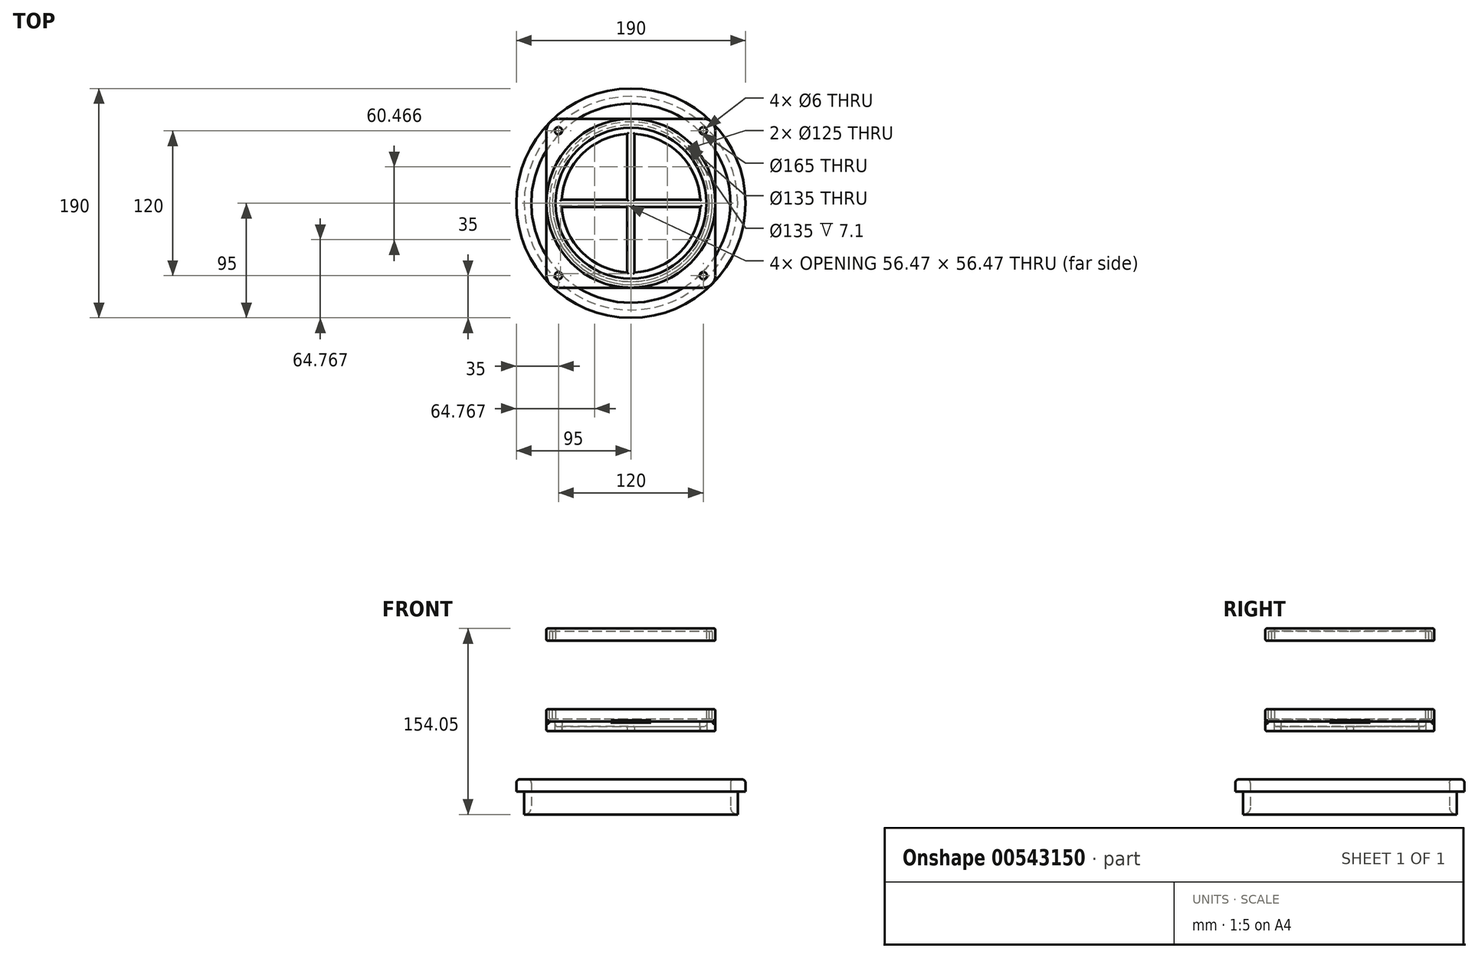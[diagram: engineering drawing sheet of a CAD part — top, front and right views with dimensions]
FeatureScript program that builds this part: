
annotation { "Feature Type Name" : "Feature", "Feature Type Description" : "" }
export const myFeature = defineFeature(function(context is Context, id is Id, definition is map)
    precondition{}
    {
        {
            var Q0;
            Q0=qCreatedBy(makeId("Top.planeOp"),FACE);
            var sketch = newSketch(context, id + "F0", { "sketchPlane" : qUnion([Q0])});
            skLineSegment(sketch, "E0.bottom", {"start": v(-60, 70) * mm, "end": v(60, 70) * mm});
            skLineSegment(sketch, "E0.top", {"start": v(-60, -70) * mm, "end": v(60, -70) * mm});
            skLineSegment(sketch, "E0.left", {"start": v(-70, 60) * mm, "end": v(-70, -60) * mm});
            skLineSegment(sketch, "E0.right", {"start": v(70, 60) * mm, "end": v(70, -60) * mm});
            skCircle(sketch, "E1", {"center": v(-60, 60) * mm, "radius": 3 * mm});
            skCircle(sketch, "E2.MirrorC", {"center": v(60, 60) * mm, "radius": 3 * mm});
            skCircle(sketch, "E3.MirrorC", {"center": v(60, -60) * mm, "radius": 3 * mm});
            skCircle(sketch, "E4.MirrorC", {"center": v(-60, -60) * mm, "radius": 3 * mm});
            skPoint(sketch, "E5.visualSharp", {"position": v(-70, -70) * mm});
            skArc(sketch, "E5.filletArc", {"start": v(-70, -60) * mm, "mid": v(-67.07, -67.07) * mm, "end": v(-60, -70) * mm});
            skPoint(sketch, "E6.visualSharp", {"position": v(-70, 70) * mm});
            skArc(sketch, "E6.filletArc", {"start": v(-60, 70) * mm, "mid": v(-67.07, 67.07) * mm, "end": v(-70, 60) * mm});
            skPoint(sketch, "E7.visualSharp", {"position": v(70, 70) * mm});
            skArc(sketch, "E7.filletArc", {"start": v(70, 60) * mm, "mid": v(67.07, 67.07) * mm, "end": v(60, 70) * mm});
            skPoint(sketch, "E8.visualSharp", {"position": v(70, -70) * mm});
            skArc(sketch, "E8.filletArc", {"start": v(60, -70) * mm, "mid": v(67.07, -67.07) * mm, "end": v(70, -60) * mm});
            skSolve(sketch);
        }
        {
            var Q0;
            Q0 = qSketchRegion(id + "F0", true);
            extrude(context, id + "F1", {"entities" : qUnion([Q0]), "depth" : 8 * mm, "offsetDistance" : 25 * mm});
        }
        {
            var Q0;
            Q0=makeQuery(id+"F1.opExtrude","CAP_FACE",FACE,{"disambiguationData":[OSD([sQuery(id+"F0.wireOp",EDGE,"E0.bottom"),sQuery(id+"F0.wireOp",EDGE,"E0.top"),sQuery(id+"F0.wireOp",EDGE,"E0.left"),sQuery(id+"F0.wireOp",EDGE,"E0.right"),sQuery(id+"F0.wireOp",EDGE,"E1"),sQuery(id+"F0.wireOp",EDGE,"E2.MirrorC"),sQuery(id+"F0.wireOp",EDGE,"E3.MirrorC"),sQuery(id+"F0.wireOp",EDGE,"E4.MirrorC"),sQuery(id+"F0.wireOp",EDGE,"E5.filletArc"),sQuery(id+"F0.wireOp",EDGE,"E6.filletArc"),sQuery(id+"F0.wireOp",EDGE,"E7.filletArc"),sQuery(id+"F0.wireOp",EDGE,"E8.filletArc"),sQuery(id+"F0.wireOp",EDGE,"JWdlXrcp-rO1S-G7ss-JCTR-8tZBUIbzlGE1")])],"isStart":false});
            var sketch = newSketch(context, id + "F2", { "sketchPlane" : qUnion([Q0])});
            skCircle(sketch, "E9", {"center": v(0, 0) * mm, "radius": 70 * mm});
            skCircle(sketch, "E10", {"center": v(0, 0) * mm, "radius": 62.5 * mm});
            skSolve(sketch);
        }
        {
            var Q0;
            Q0 = qSketchRegion(id + "F2", true);
            extrude(context, id + "F3", {"entities" : qUnion([Q0]), "operationType" : NewBodyOperationType.ADD, "depth" : 10 * mm, "offsetDistance" : 25 * mm});
        }
        {
            var Q0;
            Q0=makeQuery(id+"F2.imprint","IMPRINT",FACE,{"disambiguationData":[TD([[makeQuery(id+"F2.imprint","IMPRINT",EDGE,{"derivedFrom":sQuery(id+"F2.wireOp",EDGE,"E10")}),1.0]])]});
            var sketch = newSketch(context, id + "F4", { "sketchPlane" : qUnion([Q0])});
            skCircle(sketch, "E11", {"center": v(0, 0) * mm, "radius": 62.5 * mm});
            skSolve(sketch);
        }
        {
            var Q0;
            Q0 = qSketchRegion(id + "F4", true);
            extrude(context, id + "F5", {"entities" : qUnion([Q0]), "operationType" : NewBodyOperationType.REMOVE, "oppositeDirection" : true, "depth" : 25 * mm, "offsetDistance" : 25 * mm});
        }
        {
            var Q0;
            Q0=makeQuery(id+"F3.opExtrude","CAP_FACE",FACE,{"disambiguationData":[OSD([sQuery(id+"F2.wireOp",EDGE,"E9"),sQuery(id+"F2.wireOp",EDGE,"E10")])],"isStart":false});
            var sketch = newSketch(context, id + "F6", { "sketchPlane" : qUnion([Q0])});
            skCircle(sketch, "E12", {"center": v(0, 0) * mm, "radius": 67.5 * mm});
            skCircle(sketch, "E13", {"center": v(0, 0) * mm, "radius": 65 * mm});
            skSolve(sketch);
        }
        {
            var Q0;
            Q0 = qSketchRegion(id + "F6", true);
            extrude(context, id + "F7", {"entities" : qUnion([Q0]), "operationType" : NewBodyOperationType.REMOVE, "oppositeDirection" : true, "depth" : 8 * mm, "offsetDistance" : 25 * mm});
        }
        {
            var Q0;
            Q0=makeQuery(id+"F3.opExtrude","CAP_EDGE",EDGE,{"disambiguationData":[OSD([sQuery(id+"F2.wireOp",EDGE,"E9")])],"isStart":false});
            var Q1;
            Q1=makeQuery(id+"F7.boolean.opBoolean","COPY",EDGE,{"derivedFrom":makeQuery(id+"F7.opExtrude","CAP_EDGE",EDGE,{"disambiguationData":[OSD([sQuery(id+"F6.wireOp",EDGE,"E12")])],"isStart":true})});
            var Q2;
            Q2=makeQuery(id+"F7.boolean.opBoolean","COPY",EDGE,{"derivedFrom":makeQuery(id+"F7.opExtrude","CAP_EDGE",EDGE,{"disambiguationData":[OSD([sQuery(id+"F6.wireOp",EDGE,"E13")])],"isStart":true})});
            var Q3;
            Q3=makeQuery(id+"F3.opExtrude","CAP_EDGE",EDGE,{"disambiguationData":[OSD([sQuery(id+"F2.wireOp",EDGE,"E10")])],"isStart":false});
            var Q4;
            {var subQ0=sQuery(id+"F0.wireOp",EDGE,"E6.filletArc");var subQ1=sQuery(id+"F0.wireOp",EDGE,"E0.left");Q4=makeQuery(id+"F3.boolean.opBoolean","SPLIT",EDGE,{"disambiguationData":[TD([makeQuery(id+"F1.opExtrude","SWEPT_FACE",FACE,{"disambiguationData":[OSD([subQ0])]})])],"derivedFrom":makeQuery(id+"F1.opExtrude","CAP_EDGE",EDGE,{"disambiguationData":[OSD([subQ1])],"isStart":false})});}
            var Q5;
            {var subQ0=sQuery(id+"F0.wireOp",EDGE,"E0.left");var subQ1=sQuery(id+"F0.wireOp",EDGE,"E0.top");var subQ2=sQuery(id+"F2.wireOp",EDGE,"E9");Q5=makeQuery(id+"F3.boolean.opBoolean","SPLIT",EDGE,{"disambiguationData":[TD([makeQuery(id+"F1.opExtrude","CAP_FACE",FACE,{"disambiguationData":[OSD([sQuery(id+"F0.wireOp",EDGE,"E0.bottom"),subQ1,subQ0,sQuery(id+"F0.wireOp",EDGE,"E0.right"),sQuery(id+"F0.wireOp",EDGE,"E1"),sQuery(id+"F0.wireOp",EDGE,"E2.MirrorC"),sQuery(id+"F0.wireOp",EDGE,"E3.MirrorC"),sQuery(id+"F0.wireOp",EDGE,"E4.MirrorC"),sQuery(id+"F0.wireOp",EDGE,"E5.filletArc"),sQuery(id+"F0.wireOp",EDGE,"E6.filletArc"),sQuery(id+"F0.wireOp",EDGE,"E7.filletArc"),sQuery(id+"F0.wireOp",EDGE,"E8.filletArc")])],"isStart":false}),makeQuery(id+"F1.opExtrude","SWEPT_FACE",FACE,{"disambiguationData":[OSD([subQ1])]}),makeQuery(id+"F1.opExtrude","SWEPT_FACE",FACE,{"disambiguationData":[OSD([subQ0])]}),makeQuery(id+"F3.opExtrude","SWEPT_FACE",FACE,{"disambiguationData":[OSD([subQ2])]})])],"derivedFrom":makeQuery(id+"F3.opExtrude","CAP_EDGE",EDGE,{"disambiguationData":[OSD([subQ2])],"isStart":true})});}
            var Q6;
            Q6=makeQuery(id+"F1.opExtrude","CAP_FACE",FACE,{"disambiguationData":[OSD([sQuery(id+"F0.wireOp",EDGE,"E0.bottom"),sQuery(id+"F0.wireOp",EDGE,"E0.top"),sQuery(id+"F0.wireOp",EDGE,"E0.left"),sQuery(id+"F0.wireOp",EDGE,"E0.right"),sQuery(id+"F0.wireOp",EDGE,"E1"),sQuery(id+"F0.wireOp",EDGE,"E2.MirrorC"),sQuery(id+"F0.wireOp",EDGE,"E3.MirrorC"),sQuery(id+"F0.wireOp",EDGE,"E4.MirrorC"),sQuery(id+"F0.wireOp",EDGE,"E5.filletArc"),sQuery(id+"F0.wireOp",EDGE,"E6.filletArc"),sQuery(id+"F0.wireOp",EDGE,"E7.filletArc"),sQuery(id+"F0.wireOp",EDGE,"E8.filletArc")])],"isStart":true});
            var Q7;
            {var subQ0=sQuery(id+"F0.wireOp",EDGE,"E8.filletArc");var subQ1=sQuery(id+"F0.wireOp",EDGE,"E0.top");Q7=makeQuery(id+"F3.boolean.opBoolean","SPLIT",EDGE,{"disambiguationData":[TD([makeQuery(id+"F1.opExtrude","SWEPT_FACE",FACE,{"disambiguationData":[OSD([subQ0])]})])],"derivedFrom":makeQuery(id+"F1.opExtrude","CAP_EDGE",EDGE,{"disambiguationData":[OSD([subQ1])],"isStart":false})});}
            var Q8;
            {var subQ0=sQuery(id+"F0.wireOp",EDGE,"E0.right");var subQ1=sQuery(id+"F0.wireOp",EDGE,"E3.MirrorC");var subQ2=sQuery(id+"F0.wireOp",EDGE,"E0.top");var subQ3=sQuery(id+"F0.wireOp",EDGE,"E8.filletArc");var subQ4=makeQuery(id+"F1.opExtrude","CAP_FACE",FACE,{"disambiguationData":[OSD([sQuery(id+"F0.wireOp",EDGE,"E0.bottom"),subQ2,sQuery(id+"F0.wireOp",EDGE,"E0.left"),subQ0,sQuery(id+"F0.wireOp",EDGE,"E1"),sQuery(id+"F0.wireOp",EDGE,"E2.MirrorC"),subQ1,sQuery(id+"F0.wireOp",EDGE,"E4.MirrorC"),sQuery(id+"F0.wireOp",EDGE,"E5.filletArc"),sQuery(id+"F0.wireOp",EDGE,"E6.filletArc"),sQuery(id+"F0.wireOp",EDGE,"E7.filletArc"),subQ3])],"isStart":false});Q8=makeQuery(id+"F3.boolean.opBoolean","SPLIT",FACE,{"disambiguationData":[TD([makeQuery(id+"F1.opExtrude","SWEPT_FACE",FACE,{"disambiguationData":[OSD([subQ1])]})])],"derivedFrom":subQ4});}
            var Q9;
            {var subQ0=sQuery(id+"F0.wireOp",EDGE,"E4.MirrorC");var subQ1=sQuery(id+"F0.wireOp",EDGE,"E0.left");var subQ2=sQuery(id+"F0.wireOp",EDGE,"E0.top");var subQ3=sQuery(id+"F0.wireOp",EDGE,"E5.filletArc");var subQ4=makeQuery(id+"F1.opExtrude","CAP_FACE",FACE,{"disambiguationData":[OSD([sQuery(id+"F0.wireOp",EDGE,"E0.bottom"),subQ2,subQ1,sQuery(id+"F0.wireOp",EDGE,"E0.right"),sQuery(id+"F0.wireOp",EDGE,"E1"),sQuery(id+"F0.wireOp",EDGE,"E2.MirrorC"),sQuery(id+"F0.wireOp",EDGE,"E3.MirrorC"),subQ0,subQ3,sQuery(id+"F0.wireOp",EDGE,"E6.filletArc"),sQuery(id+"F0.wireOp",EDGE,"E7.filletArc"),sQuery(id+"F0.wireOp",EDGE,"E8.filletArc")])],"isStart":false});Q9=makeQuery(id+"F3.boolean.opBoolean","SPLIT",FACE,{"disambiguationData":[TD([makeQuery(id+"F1.opExtrude","SWEPT_FACE",FACE,{"disambiguationData":[OSD([subQ0])]})])],"derivedFrom":subQ4});}
            var Q10;
            {var subQ0=sQuery(id+"F0.wireOp",EDGE,"E2.MirrorC");var subQ1=sQuery(id+"F0.wireOp",EDGE,"E7.filletArc");var subQ2=sQuery(id+"F0.wireOp",EDGE,"E0.right");var subQ3=sQuery(id+"F0.wireOp",EDGE,"E0.bottom");var subQ4=makeQuery(id+"F1.opExtrude","CAP_FACE",FACE,{"disambiguationData":[OSD([subQ3,sQuery(id+"F0.wireOp",EDGE,"E0.top"),sQuery(id+"F0.wireOp",EDGE,"E0.left"),subQ2,sQuery(id+"F0.wireOp",EDGE,"E1"),subQ0,sQuery(id+"F0.wireOp",EDGE,"E3.MirrorC"),sQuery(id+"F0.wireOp",EDGE,"E4.MirrorC"),sQuery(id+"F0.wireOp",EDGE,"E5.filletArc"),sQuery(id+"F0.wireOp",EDGE,"E6.filletArc"),subQ1,sQuery(id+"F0.wireOp",EDGE,"E8.filletArc")])],"isStart":false});Q10=makeQuery(id+"F3.boolean.opBoolean","SPLIT",FACE,{"disambiguationData":[TD([makeQuery(id+"F1.opExtrude","SWEPT_FACE",FACE,{"disambiguationData":[OSD([subQ0])]})])],"derivedFrom":subQ4});}
            var Q11;
            {var subQ0=sQuery(id+"F0.wireOp",EDGE,"E1");var subQ1=sQuery(id+"F0.wireOp",EDGE,"E0.left");var subQ2=sQuery(id+"F0.wireOp",EDGE,"E6.filletArc");var subQ3=sQuery(id+"F0.wireOp",EDGE,"E0.bottom");var subQ4=makeQuery(id+"F1.opExtrude","CAP_FACE",FACE,{"disambiguationData":[OSD([subQ3,sQuery(id+"F0.wireOp",EDGE,"E0.top"),subQ1,sQuery(id+"F0.wireOp",EDGE,"E0.right"),subQ0,sQuery(id+"F0.wireOp",EDGE,"E2.MirrorC"),sQuery(id+"F0.wireOp",EDGE,"E3.MirrorC"),sQuery(id+"F0.wireOp",EDGE,"E4.MirrorC"),sQuery(id+"F0.wireOp",EDGE,"E5.filletArc"),subQ2,sQuery(id+"F0.wireOp",EDGE,"E7.filletArc"),sQuery(id+"F0.wireOp",EDGE,"E8.filletArc")])],"isStart":false});Q11=makeQuery(id+"F3.boolean.opBoolean","SPLIT",FACE,{"disambiguationData":[TD([makeQuery(id+"F1.opExtrude","SWEPT_FACE",FACE,{"disambiguationData":[OSD([subQ0])]})])],"derivedFrom":subQ4});}
            fillet(context, id + "F8", {"entities" : qUnion([Q0, Q1, Q2, Q3, Q4, Q5, Q6, Q7, Q8, Q9, Q10, Q11]), "tangentPropagation" : true, "radius" : 1 * mm, "defaultsChanged" : false, "vertexSettings" : [], "allowEdgeOverflow" : false});
        }
        {
            var Q0;
            Q0=makeQuery(id+"F7.boolean.opBoolean","COPY",EDGE,{"derivedFrom":makeQuery(id+"F7.opExtrude","CAP_EDGE",EDGE,{"disambiguationData":[OSD([sQuery(id+"F6.wireOp",EDGE,"E12")])],"isStart":false})});
            var Q1;
            Q1=makeQuery(id+"F7.boolean.opBoolean","COPY",EDGE,{"derivedFrom":makeQuery(id+"F7.opExtrude","CAP_EDGE",EDGE,{"disambiguationData":[OSD([sQuery(id+"F6.wireOp",EDGE,"E13")])],"isStart":false})});
            fillet(context, id + "F9", {"entities" : qUnion([Q0, Q1]), "tangentPropagation" : true, "radius" : 0.9 * mm, "defaultsChanged" : true, "vertexSettings" : [], "allowEdgeOverflow" : false});
        }
        {
            var Q0;
            Q0=qCreatedBy(makeId("Top.planeOp"),FACE);
            cPlane(context, id + "F10", {"entities" : qUnion([Q0]), "cplaneType" : CPlaneType.OFFSET, "offset" : 75 * mm, "width" : 150 * mm, "height" : 150 * mm});
        }
        {
            var Q0;
            Q0=qCreatedBy(id+"F10.planeOp",FACE);
            var sketch = newSketch(context, id + "F11", { "sketchPlane" : qUnion([Q0])});
            skCircle(sketch, "E14", {"center": v(0, 0) * mm, "radius": 62.5 * mm});
            skCircle(sketch, "E15", {"center": v(0, 0) * mm, "radius": 70 * mm});
            skSolve(sketch);
        }
        {
            var Q0;
            Q0 = qSketchRegion(id + "F11", true);
            extrude(context, id + "F12", {"entities" : qUnion([Q0]), "depth" : 10 * mm, "offsetDistance" : 25 * mm});
        }
        {
            var Q0;
            Q0=makeQuery(id+"F12.opExtrude","CAP_FACE",FACE,{"disambiguationData":[OSD([sQuery(id+"F11.wireOp",EDGE,"E14"),sQuery(id+"F11.wireOp",EDGE,"E15")])],"isStart":true});
            var sketch = newSketch(context, id + "F13", { "sketchPlane" : qUnion([Q0])});
            skCircle(sketch, "E16", {"center": v(0, 0) * mm, "radius": 65 * mm});
            skCircle(sketch, "E17", {"center": v(0, 0) * mm, "radius": 67.5 * mm});
            skSolve(sketch);
        }
        {
            var Q0;
            Q0 = qSketchRegion(id + "F13", true);
            extrude(context, id + "F14", {"entities" : qUnion([Q0]), "operationType" : NewBodyOperationType.REMOVE, "oppositeDirection" : true, "depth" : 8 * mm, "offsetDistance" : 25 * mm});
        }
        {
            var Q0;
            Q0=makeQuery(id+"F1.opExtrude","CAP_FACE",FACE,{"disambiguationData":[OSD([sQuery(id+"F0.wireOp",EDGE,"E0.bottom"),sQuery(id+"F0.wireOp",EDGE,"E0.top"),sQuery(id+"F0.wireOp",EDGE,"E0.left"),sQuery(id+"F0.wireOp",EDGE,"E0.right"),sQuery(id+"F0.wireOp",EDGE,"E1"),sQuery(id+"F0.wireOp",EDGE,"E2.MirrorC"),sQuery(id+"F0.wireOp",EDGE,"E3.MirrorC"),sQuery(id+"F0.wireOp",EDGE,"E4.MirrorC"),sQuery(id+"F0.wireOp",EDGE,"E5.filletArc"),sQuery(id+"F0.wireOp",EDGE,"E6.filletArc"),sQuery(id+"F0.wireOp",EDGE,"E7.filletArc"),sQuery(id+"F0.wireOp",EDGE,"E8.filletArc")])],"isStart":true});
            var sketch = newSketch(context, id + "F15", { "sketchPlane" : qUnion([Q0])});
            skCircle(sketch, "E18", {"center": v(0, 0) * mm, "radius": 67.5 * mm});
            skArc(sketch, "E19", {"start": v(-57.42, -3) * mm, "mid": v(-40.66, -40.66) * mm, "end": v(-3, -57.42) * mm});
            skLineSegment(sketch, "E20", {"start": v(3, 57.42) * mm, "end": v(3, 3) * mm});
            skLineSegment(sketch, "E21", {"start": v(3, 3) * mm, "end": v(57.42, 3) * mm});
            skLineSegment(sketch, "E22", {"start": v(3, -3) * mm, "end": v(57.42, -3) * mm});
            skLineSegment(sketch, "E23.trimOffspring", {"start": v(3, -3) * mm, "end": v(3, -57.42) * mm});
            skLineSegment(sketch, "E24.MirrorCS", {"start": v(-3, -3) * mm, "end": v(-3, -57.42) * mm});
            skLineSegment(sketch, "E25.MirrorCS", {"start": v(-3, -3) * mm, "end": v(-57.42, -3) * mm});
            skLineSegment(sketch, "E26.MirrorCS", {"start": v(-3, 3) * mm, "end": v(-57.42, 3) * mm});
            skLineSegment(sketch, "E27.MirrorCS", {"start": v(-3, 57.42) * mm, "end": v(-3, 3) * mm});
            skArc(sketch, "E28.trimOffspring", {"start": v(-3, 57.42) * mm, "mid": v(-40.66, 40.66) * mm, "end": v(-57.42, 3) * mm});
            skArc(sketch, "E29.trimOffspring", {"start": v(57.42, 3) * mm, "mid": v(40.66, 40.66) * mm, "end": v(3, 57.42) * mm});
            skArc(sketch, "E30.trimOffspring", {"start": v(3, -57.42) * mm, "mid": v(40.66, -40.66) * mm, "end": v(57.42, -3) * mm});
            skSolve(sketch);
        }
        {
            var Q0;
            Q0 = qSketchRegion(id + "F15", true);
            extrude(context, id + "F16", {"entities" : qUnion([Q0]), "operationType" : NewBodyOperationType.ADD, "oppositeDirection" : true, "depth" : 4 * mm, "offsetDistance" : 25 * mm});
        }
        {
            var Q0;
            Q0=makeQuery(id+"F16.opExtrude","CAP_FACE",FACE,{"disambiguationData":[OSD([sQuery(id+"F15.wireOp",EDGE,"E18"),sQuery(id+"F15.wireOp",EDGE,"E19"),sQuery(id+"F15.wireOp",EDGE,"E20"),sQuery(id+"F15.wireOp",EDGE,"E21"),sQuery(id+"F15.wireOp",EDGE,"E22"),sQuery(id+"F15.wireOp",EDGE,"E23.trimOffspring"),sQuery(id+"F15.wireOp",EDGE,"E24.MirrorCS"),sQuery(id+"F15.wireOp",EDGE,"E25.MirrorCS"),sQuery(id+"F15.wireOp",EDGE,"E26.MirrorCS"),sQuery(id+"F15.wireOp",EDGE,"E27.MirrorCS"),sQuery(id+"F15.wireOp",EDGE,"E28.trimOffspring"),sQuery(id+"F15.wireOp",EDGE,"E29.trimOffspring"),sQuery(id+"F15.wireOp",EDGE,"E30.trimOffspring")])],"isStart":false});
            var Q1;
            Q1=makeQuery(id+"F16.boolean.opBoolean","MERGE",FACE,{"derivedFrom":[makeQuery(id+"F1.opExtrude","CAP_FACE",FACE,{"disambiguationData":[OSD([sQuery(id+"F0.wireOp",EDGE,"E0.bottom"),sQuery(id+"F0.wireOp",EDGE,"E0.top"),sQuery(id+"F0.wireOp",EDGE,"E0.left"),sQuery(id+"F0.wireOp",EDGE,"E0.right"),sQuery(id+"F0.wireOp",EDGE,"E1"),sQuery(id+"F0.wireOp",EDGE,"E2.MirrorC"),sQuery(id+"F0.wireOp",EDGE,"E3.MirrorC"),sQuery(id+"F0.wireOp",EDGE,"E4.MirrorC"),sQuery(id+"F0.wireOp",EDGE,"E5.filletArc"),sQuery(id+"F0.wireOp",EDGE,"E6.filletArc"),sQuery(id+"F0.wireOp",EDGE,"E7.filletArc"),sQuery(id+"F0.wireOp",EDGE,"E8.filletArc")])],"isStart":true}),makeQuery(id+"F16.opExtrude","CAP_FACE",FACE,{"disambiguationData":[OSD([sQuery(id+"F15.wireOp",EDGE,"E18"),sQuery(id+"F15.wireOp",EDGE,"E19"),sQuery(id+"F15.wireOp",EDGE,"E20"),sQuery(id+"F15.wireOp",EDGE,"E21"),sQuery(id+"F15.wireOp",EDGE,"E22"),sQuery(id+"F15.wireOp",EDGE,"E23.trimOffspring"),sQuery(id+"F15.wireOp",EDGE,"E24.MirrorCS"),sQuery(id+"F15.wireOp",EDGE,"E25.MirrorCS"),sQuery(id+"F15.wireOp",EDGE,"E26.MirrorCS"),sQuery(id+"F15.wireOp",EDGE,"E27.MirrorCS"),sQuery(id+"F15.wireOp",EDGE,"E28.trimOffspring"),sQuery(id+"F15.wireOp",EDGE,"E29.trimOffspring"),sQuery(id+"F15.wireOp",EDGE,"E30.trimOffspring")])],"isStart":true})]});
            fillet(context, id + "F17", {"entities" : qUnion([Q0, Q1]), "tangentPropagation" : true, "radius" : 1 * mm, "defaultsChanged" : false, "vertexSettings" : [], "allowEdgeOverflow" : false});
        }
        {
            var Q0;
            {var subQ0=sQuery(id+"F11.wireOp",EDGE,"E15");Q0=makeQuery(id+"F14.boolean.opBoolean","SPLIT",FACE,{"disambiguationData":[TD([makeQuery(id+"F12.opExtrude","SWEPT_FACE",FACE,{"disambiguationData":[OSD([subQ0])]})])],"derivedFrom":makeQuery(id+"F12.opExtrude","CAP_FACE",FACE,{"disambiguationData":[OSD([sQuery(id+"F11.wireOp",EDGE,"E14"),subQ0])],"isStart":true})});}
            var Q1;
            {var subQ0=sQuery(id+"F11.wireOp",EDGE,"E14");Q1=makeQuery(id+"F14.boolean.opBoolean","SPLIT",FACE,{"disambiguationData":[TD([makeQuery(id+"F12.opExtrude","SWEPT_FACE",FACE,{"disambiguationData":[OSD([subQ0])]})])],"derivedFrom":makeQuery(id+"F12.opExtrude","CAP_FACE",FACE,{"disambiguationData":[OSD([subQ0,sQuery(id+"F11.wireOp",EDGE,"E15")])],"isStart":true})});}
            var Q2;
            Q2=makeQuery(id+"F14.boolean.opBoolean","COPY",FACE,{"derivedFrom":makeQuery(id+"F14.opExtrude","CAP_FACE",FACE,{"disambiguationData":[OSD([sQuery(id+"F13.wireOp",EDGE,"E16"),sQuery(id+"F13.wireOp",EDGE,"E17")])],"isStart":false})});
            var Q3;
            Q3=makeQuery(id+"F12.opExtrude","CAP_FACE",FACE,{"disambiguationData":[OSD([sQuery(id+"F11.wireOp",EDGE,"E14"),sQuery(id+"F11.wireOp",EDGE,"E15")])],"isStart":false});
            fillet(context, id + "F18", {"entities" : qUnion([Q0, Q1, Q2, Q3]), "tangentPropagation" : true, "radius" : 1 * mm, "defaultsChanged" : false, "vertexSettings" : [], "allowEdgeOverflow" : false});
        }
        {
            var Q0;
            Q0=qCreatedBy(makeId("Top.planeOp"),FACE);
            cPlane(context, id + "F19", {"entities" : qUnion([Q0]), "cplaneType" : CPlaneType.OFFSET, "offset" : 50 * mm, "oppositeDirection" : true, "width" : 150 * mm, "height" : 150 * mm});
        }
        {
            var Q0;
            Q0=qCreatedBy(id+"F19.planeOp",FACE);
            var sketch = newSketch(context, id + "F20", { "sketchPlane" : qUnion([Q0])});
            skCircle(sketch, "E31", {"center": v(0, 0) * mm, "radius": 95 * mm});
            skCircle(sketch, "E32", {"center": v(0, 0) * mm, "radius": 82.5 * mm});
            skSolve(sketch);
        }
        {
            var Q0;
            Q0 = qSketchRegion(id + "F20", true);
            extrude(context, id + "F21", {"entities" : qUnion([Q0]), "depth" : 10 * mm, "offsetDistance" : 25 * mm});
        }
        {
            var Q0;
            Q0=makeQuery(id+"F21.opExtrude","CAP_FACE",FACE,{"disambiguationData":[OSD([sQuery(id+"F20.wireOp",EDGE,"E31"),sQuery(id+"F20.wireOp",EDGE,"E32")])],"isStart":true});
            var sketch = newSketch(context, id + "F22", { "sketchPlane" : qUnion([Q0])});
            skCircle(sketch, "E33", {"center": v(0, 0) * mm, "radius": 88.5 * mm});
            skCircle(sketch, "E34", {"center": v(0, 0) * mm, "radius": 82.5 * mm});
            skSolve(sketch);
        }
        {
            var Q0;
            Q0 = qSketchRegion(id + "F22", true);
            extrude(context, id + "F23", {"entities" : qUnion([Q0]), "operationType" : NewBodyOperationType.ADD, "depth" : 19.05 * mm, "offsetDistance" : 25 * mm});
        }
        {
            var Q0;
            Q0=makeQuery(id+"F21.opExtrude","CAP_EDGE",EDGE,{"disambiguationData":[OSD([sQuery(id+"F20.wireOp",EDGE,"E31")])],"isStart":false});
            var Q1;
            Q1=makeQuery(id+"F21.opExtrude","CAP_EDGE",EDGE,{"disambiguationData":[OSD([sQuery(id+"F20.wireOp",EDGE,"E32")])],"isStart":false});
            fillet(context, id + "F24", {"entities" : qUnion([Q0, Q1]), "tangentPropagation" : true, "radius" : 3 * mm, "defaultsChanged" : true, "vertexSettings" : [], "allowEdgeOverflow" : false});
        }
        {
            var Q0;
            Q0=makeQuery(id+"F23.opExtrude","CAP_EDGE",EDGE,{"disambiguationData":[OSD([sQuery(id+"F22.wireOp",EDGE,"E34")])],"isStart":false});
            fillet(context, id + "F25", {"entities" : qUnion([Q0]), "tangentPropagation" : true, "radius" : 6 * mm, "defaultsChanged" : true, "vertexSettings" : [], "allowEdgeOverflow" : false});
        }
    });
